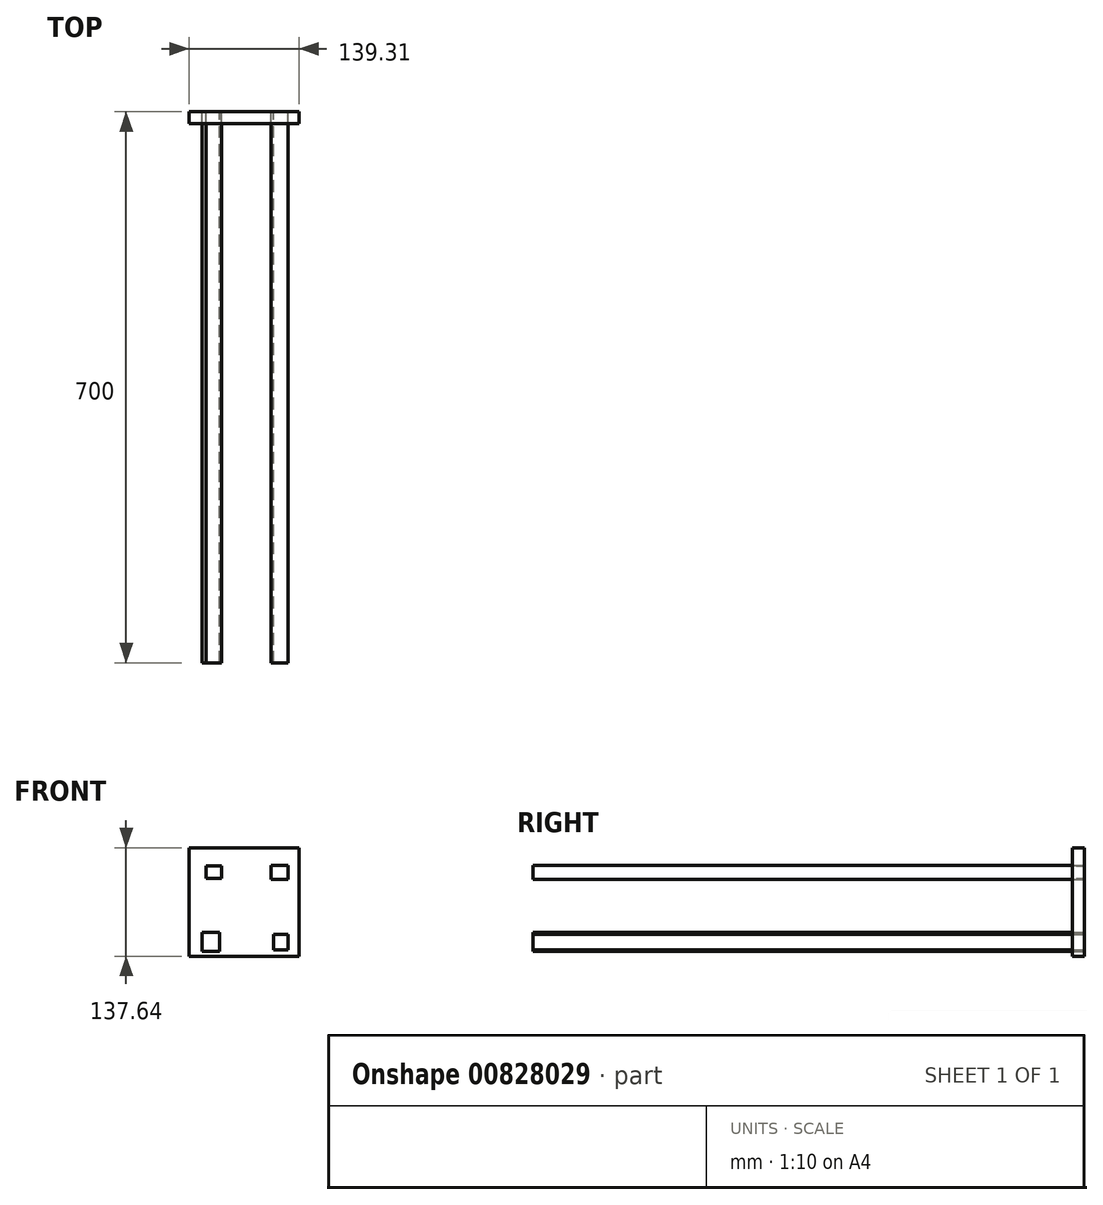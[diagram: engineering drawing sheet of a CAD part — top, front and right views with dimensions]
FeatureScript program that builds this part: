
annotation { "Feature Type Name" : "Feature", "Feature Type Description" : "" }
export const myFeature = defineFeature(function(context is Context, id is Id, definition is map)
    precondition{}
    {
        {
            var Q0;
            Q0=qCreatedBy(makeId("Front.planeOp"),FACE);
            var sketch = newSketch(context, id + "F0", { "sketchPlane" : qUnion([Q0])});
            skLineSegment(sketch, "E0.bottom", {"start": v(-49.1, 47.28) * mm, "end": v(-29.1, 47.28) * mm});
            skLineSegment(sketch, "E0.top", {"start": v(-49.1, 31.28) * mm, "end": v(-29.1, 31.28) * mm});
            skLineSegment(sketch, "E0.left", {"start": v(-49.1, 47.28) * mm, "end": v(-49.1, 31.28) * mm});
            skLineSegment(sketch, "E0.right", {"start": v(-29.1, 47.28) * mm, "end": v(-29.1, 31.28) * mm});
            skLineSegment(sketch, "E1.bottom", {"start": v(33.46, 47.65) * mm, "end": v(55.29, 47.65) * mm});
            skLineSegment(sketch, "E1.top", {"start": v(33.46, 29.83) * mm, "end": v(55.29, 29.83) * mm});
            skLineSegment(sketch, "E1.left", {"start": v(33.46, 47.65) * mm, "end": v(33.46, 29.83) * mm});
            skLineSegment(sketch, "E1.right", {"start": v(55.29, 47.65) * mm, "end": v(55.29, 29.83) * mm});
            skLineSegment(sketch, "E2.bottom", {"start": v(36.74, -39.65) * mm, "end": v(55.29, -39.65) * mm});
            skLineSegment(sketch, "E2.top", {"start": v(36.74, -59.65) * mm, "end": v(55.29, -59.65) * mm});
            skLineSegment(sketch, "E2.left", {"start": v(36.74, -39.65) * mm, "end": v(36.74, -59.65) * mm});
            skLineSegment(sketch, "E2.right", {"start": v(55.29, -39.65) * mm, "end": v(55.29, -59.65) * mm});
            skLineSegment(sketch, "E3.bottom", {"start": v(-53.83, -37.1) * mm, "end": v(-31.64, -37.1) * mm});
            skLineSegment(sketch, "E3.top", {"start": v(-53.83, -61.47) * mm, "end": v(-31.64, -61.47) * mm});
            skLineSegment(sketch, "E3.left", {"start": v(-53.83, -37.1) * mm, "end": v(-53.83, -61.47) * mm});
            skLineSegment(sketch, "E3.right", {"start": v(-31.64, -37.1) * mm, "end": v(-31.64, -61.47) * mm});
            skSolve(sketch);
        }
        {
            var Q0;
            Q0=makeQuery(id+"F0.imprint","IMPRINT",FACE,{"disambiguationData":[TD([[makeQuery(id+"F0.imprint","IMPRINT",EDGE,{"derivedFrom":sQuery(id+"F0.wireOp",EDGE,"E3.bottom")}),-1.0]])]});
            var Q1;
            Q1=makeQuery(id+"F0.imprint","IMPRINT",FACE,{"disambiguationData":[TD([[makeQuery(id+"F0.imprint","IMPRINT",EDGE,{"derivedFrom":sQuery(id+"F0.wireOp",EDGE,"E2.bottom")}),-1.0]])]});
            var Q2;
            Q2=makeQuery(id+"F0.imprint","IMPRINT",FACE,{"disambiguationData":[TD([[makeQuery(id+"F0.imprint","IMPRINT",EDGE,{"derivedFrom":sQuery(id+"F0.wireOp",EDGE,"E1.bottom")}),-1.0]])]});
            var Q3;
            Q3=makeQuery(id+"F0.imprint","IMPRINT",FACE,{"disambiguationData":[TD([[makeQuery(id+"F0.imprint","IMPRINT",EDGE,{"derivedFrom":sQuery(id+"F0.wireOp",EDGE,"E0.bottom")}),-1.0]])]});
            extrude(context, id + "F1", {"entities" : qUnion([Q0, Q1, Q2, Q3]), "depth" : 700 * mm, "offsetDistance" : 25 * mm});
        }
        {
            var Q0;
            Q0=qCreatedBy(makeId("Front.planeOp"),FACE);
            var sketch = newSketch(context, id + "F2", { "sketchPlane" : qUnion([Q0])});
            skLineSegment(sketch, "E4.bottom", {"start": v(69.13, 70.03) * mm, "end": v(-70.18, 70.03) * mm});
            skLineSegment(sketch, "E4.top", {"start": v(69.13, -67.6) * mm, "end": v(-70.18, -67.6) * mm});
            skLineSegment(sketch, "E4.left", {"start": v(69.13, 70.03) * mm, "end": v(69.13, -67.6) * mm});
            skLineSegment(sketch, "E4.right", {"start": v(-70.18, 70.03) * mm, "end": v(-70.18, -67.6) * mm});
            skSolve(sketch);
        }
        {
            var Q0;
            Q0=makeQuery(id+"F2.imprint","IMPRINT",FACE,{"disambiguationData":[TD([[makeQuery(id+"F2.imprint","IMPRINT",EDGE,{"derivedFrom":sQuery(id+"F2.wireOp",EDGE,"E4.bottom")}),1.0]])]});
            extrude(context, id + "F3", {"entities" : qUnion([Q0]), "depth" : 15 * mm, "offsetDistance" : 25 * mm});
        }
    });
